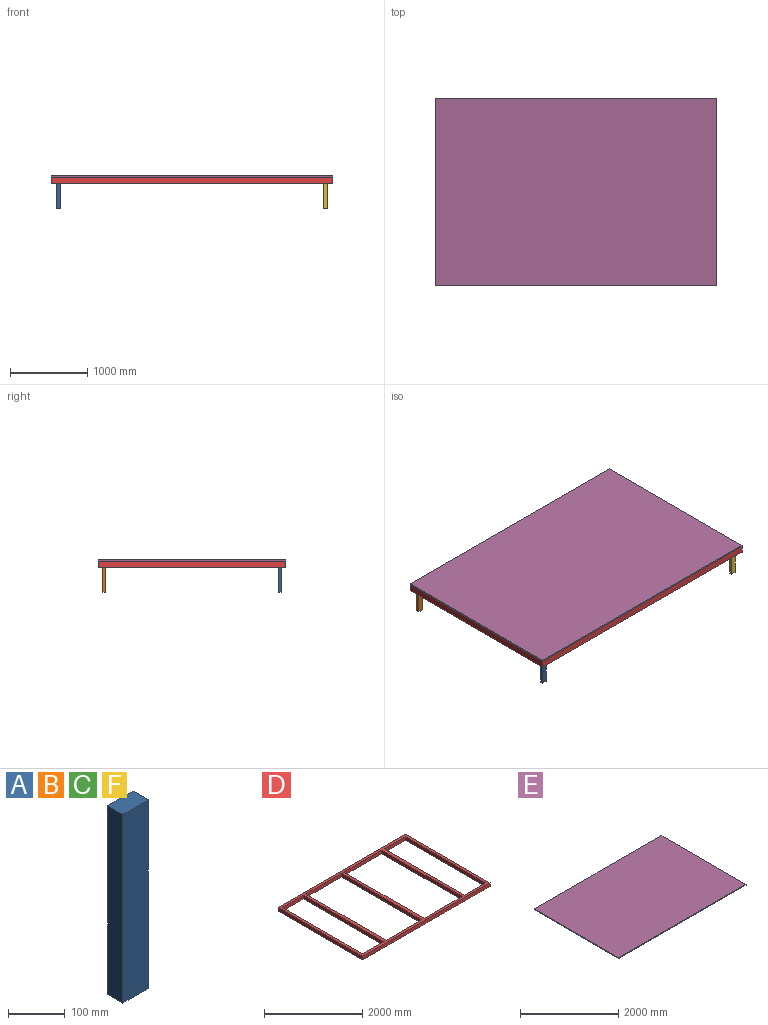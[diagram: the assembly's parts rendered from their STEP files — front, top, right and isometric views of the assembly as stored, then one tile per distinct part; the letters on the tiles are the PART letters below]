
ASSEMBLY  parts=6 mates=6
PART A: 6 faces, bbox 63.5x38.1x406.4 mm
  f0: plane 406.4x38.1mm, normal (-1,0,0), area 15483.8mm2, adj f1,f3,f4,f5
  f1: plane 63.5x38.1mm, normal (0,0,-1), area 2419.3mm2, adj f0,f2,f4,f5
  f2: plane 406.4x38.1mm, normal (1,0,0), area 15483.8mm2, adj f1,f3,f4,f5
  f3: plane 63.5x38.1mm, normal (0,0,1), area 2419.4mm2, adj f0,f2,f4,f5
  f4: plane 406.4x63.5mm, normal (0,-1,0), area 25806.4mm2, adj f0,f1,f2,f3
  f5: plane 406.4x63.5mm, normal (0,1,0), area 25806.4mm2, adj f0,f1,f2,f3
PART B: same geometry as A
PART C: same geometry as A
PART D: 22 faces, bbox 3657.6x2438.4x88.9 mm
  f0: plane 2311.4x88.9mm, normal (-1,0,0), area 205483.5mm2, adj f1,f19,f20,f21
  f1: plane 609.6x88.9mm, normal (0,1,0), area 54193.4mm2, adj f0,f2,f20,f21
  f2: plane 2311.4x88.9mm, normal (1,0,0), area 205483.5mm2, adj f1,f19,f20,f21
  f3: plane 2438.4x88.9mm, normal (-1,0,0), area 216773.8mm2, adj f4,f15,f20,f21
  f4: plane 3657.6x88.9mm, normal (0,-1,0), area 325160.6mm2, adj f3,f5,f20,f21
  f5: plane 2438.4x88.9mm, normal (1,0,0), area 216773.8mm2, adj f4,f15,f20,f21
  f6: plane 1028.7x88.9mm, normal (0,1,0), area 91451.4mm2, adj f7,f16,f20,f21
  f7: plane 2311.4x88.9mm, normal (1,0,0), area 205483.5mm2, adj f6,f8,f20,f21
  f8: plane 1028.7x88.9mm, normal (0,-1,0), area 91451.4mm2, adj f7,f16,f20,f21
  f9: plane 1092.2x88.9mm, normal (0,1,0), area 97096.6mm2, adj f10,f17,f20,f21
  f10: plane 2311.4x88.9mm, normal (1,0,0), area 205483.5mm2, adj f9,f11,f20,f21
  f11: plane 1092.2x88.9mm, normal (0,-1,0), area 97096.6mm2, adj f10,f17,f20,f21
  f12: plane 2311.4x88.9mm, normal (1,0,0), area 205483.5mm2, adj f13,f18,f20,f21
  f13: plane 609.6x88.9mm, normal (0,-1,0), area 54193.4mm2, adj f12,f14,f20,f21
  f14: plane 2311.4x88.9mm, normal (-1,0,0), area 205483.5mm2, adj f13,f18,f20,f21
  f15: plane 3657.6x88.9mm, normal (0,1,0), area 325160.6mm2, adj f3,f5,f20,f21
  f16: plane 2311.4x88.9mm, normal (-1,0,0), area 205483.5mm2, adj f6,f8,f20,f21
  f17: plane 2311.4x88.9mm, normal (-1,0,0), area 205483.5mm2, adj f9,f11,f20,f21
  f18: plane 609.6x88.9mm, normal (0,1,0), area 54193.4mm2, adj f12,f14,f20,f21
  f19: plane 609.6x88.9mm, normal (0,-1,0), area 54193.4mm2, adj f0,f2,f20,f21
  f20: plane 3657.6x2438.4mm, normal (0,0,1), area 1198384.7mm2, adj f0,f1,f2,f3,f4,f5,f6,f7
  f21: plane 3657.6x2438.4mm, normal (0,0,-1), area 1198384.7mm2, adj f0,f1,f2,f3,f4,f5,f6,f7
PART E: 6 faces, bbox 3657.6x2438.4x19.1 mm
  f0: plane 2438.4x19.05mm, normal (-1,0,0), area 46451.5mm2, adj f1,f3,f4,f5
  f1: plane 3657.6x19.05mm, normal (0,-1,0), area 69677.3mm2, adj f0,f2,f4,f5
  f2: plane 2438.4x19.05mm, normal (1,0,0), area 46451.5mm2, adj f1,f3,f4,f5
  f3: plane 3657.6x19.05mm, normal (0,1,0), area 69677.3mm2, adj f0,f2,f4,f5
  f4: plane 3657.6x2438.4mm, normal (0,0,1), area 8918691.8mm2, adj f0,f1,f2,f3
  f5: plane 3657.6x2438.4mm, normal (0,0,-1), area 8918691.8mm2, adj f0,f1,f2,f3
PART F: same geometry as A
PLACE A t=(-1328.31,1591.15,186.55)mm
PLACE B t=(-1328.31,3864.45,186.55)mm
PLACE C t=(2138.79,3864.45,186.55)mm
PLACE D t=(-1391.81,1489.55,486.65)mm
PLACE E t=(-1391.81,1489.55,575.55)mm
PLACE F t=(2138.79,1591.15,186.55)mm
MATE planar A.f4 <-> D.f1  axis (0,-1,0) through (-1296.56,1553.05,575.55)mm
MATE planar E.f1 <-> D.f4  axis (0,-1,0) through (436.99,1489.55,585.08)mm
MATE planar E.f5 <-> D.f20  axis (0,0,-1) through (436.99,2708.75,575.55)mm
MATE planar A.f0 <-> D.f2  axis (-1,0,0) through (-1328.31,1572.1,372.35)mm
MATE planar E.f0 <-> D.f3  axis (-1,0,0) through (-1391.81,2708.75,585.08)mm
MATE planar A.f3 <-> E.f5  axis (0,0,1) through (-1296.56,1572.1,575.55)mm
